# Revit family: Nero Pendant 3-686-xx email
name_source: partatom
category: Lighting Fixtures
units: mm (PartAtom-declared; Revit-internal decimal feet)

## family parameters
Always vertical = Yes
Cut with Voids When Loaded = No
Host = Ceiling
Light Source = Yes
OmniClass Number = 23.80.70.11
OmniClass Title = Luminaries for Internal Lighting
Part Type = Normal
Room Calculation Point = No
Round Connector Dimension = Use Diameter
Shared = No

## types (1)
- 3-686-15 / Black
    Color Filter = 16777215
    Default Elevation = 0 mm  [stored 0 ft]
    Diffusers = White Frost Glass
    Dimming Lamp Color Temperature Shift = <None>
    Lamp = LED Array
    Manufacturer = Oxygen - Lighting & Fans
    Metal Finish = 15 - Black
    Metal Finish 2 = 40 - Aged Brass
    Model = 3-686-xx Nero Pendant
    Photometric Web File = 3-686-1540 Nero Pendant.ies
    References = Ref. 3 = 120 V / Ref. 37 = 277 V
    Tilt Angle = 90.00°
    URL = www.oxygenlighting.com
    Voltage = 120 V
    Voltage Input = 120 V or 277 V - 50/60 Hz
    Wattage Comments = 64.32 W at 120 V

note: [stored X ft] marks values corroborated as IEEE doubles in the binary element streams (Revit-internal decimal feet)

## geometry (parser evidence)
native form markers: Blend x4, Sweep x4
no freeform markers — native parametric forms only
